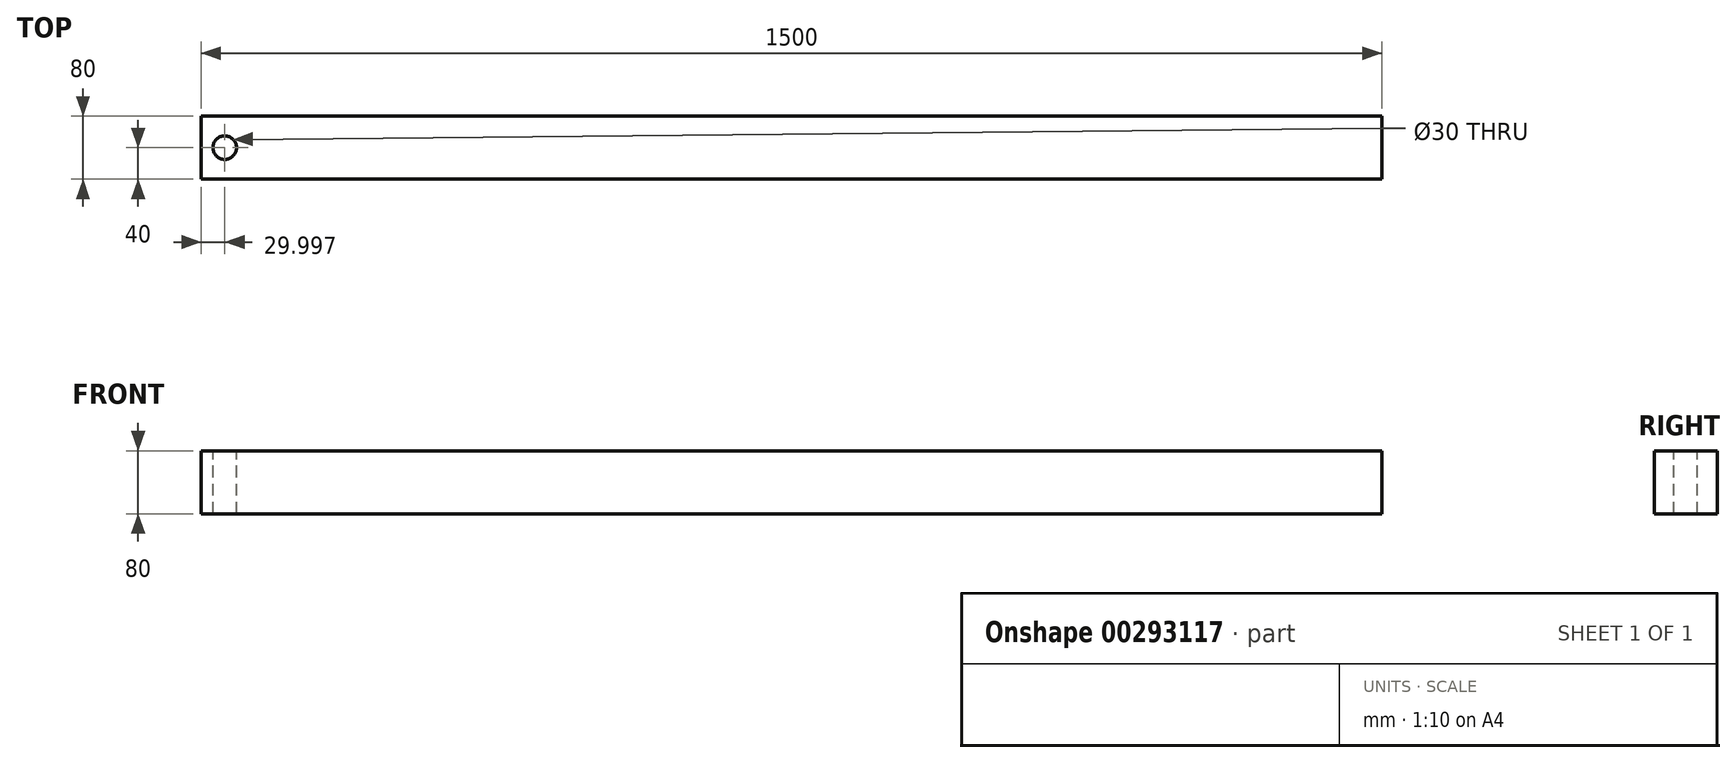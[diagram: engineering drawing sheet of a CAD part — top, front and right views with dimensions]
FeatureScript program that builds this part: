
annotation { "Feature Type Name" : "Feature", "Feature Type Description" : "" }
export const myFeature = defineFeature(function(context is Context, id is Id, definition is map)
    precondition{}
    {
        {
            var Q0;
            Q0=qCreatedBy(makeId("Top.planeOp"),FACE);
            var sketch = newSketch(context, id + "F0", { "sketchPlane" : qUnion([Q0])});
            skLineSegment(sketch, "E0.bottom", {"start": v(752.79, -40) * mm, "end": v(-747.21, -40) * mm});
            skLineSegment(sketch, "E0.top", {"start": v(752.79, 40) * mm, "end": v(-747.21, 40) * mm});
            skLineSegment(sketch, "E0.left", {"start": v(752.79, -40) * mm, "end": v(752.79, 40) * mm});
            skLineSegment(sketch, "E0.right", {"start": v(-747.21, -40) * mm, "end": v(-747.21, 40) * mm});
            skPoint(sketch, "E0.middle", {"position": v(2.79, 0) * mm});
            skSolve(sketch);
        }
        {
            var Q0;
            Q0=makeQuery(id+"F0.imprint","IMPRINT",FACE,{"disambiguationData":[TD([[makeQuery(id+"F0.imprint","IMPRINT",EDGE,{"derivedFrom":sQuery(id+"F0.wireOp",EDGE,"E0.bottom")}),-1.0]])]});
            extrude(context, id + "F1", {"entities" : qUnion([Q0]), "depth" : 80 * mm});
        }
        {
            var Q0;
            Q0=makeQuery(id+"F1.opExtrude","CAP_FACE",FACE,{"disambiguationData":[OSD([sQuery(id+"F0.wireOp",EDGE,"E0.bottom"),sQuery(id+"F0.wireOp",EDGE,"E0.top"),sQuery(id+"F0.wireOp",EDGE,"E0.left"),sQuery(id+"F0.wireOp",EDGE,"E0.right")])],"isStart":false});
            var sketch = newSketch(context, id + "F2", { "sketchPlane" : qUnion([Q0])});
            skPoint(sketch, "E1", {"position": v(-717.21, 0) * mm});
            skPoint(sketch, "E1.positionSnap0", {"position": v(-747.21, 0) * mm});
            skCircle(sketch, "E2", {"center": v(-717.21, 0) * mm, "radius": 15 * mm});
            skSolve(sketch);
        }
        {
            var Q0;
            Q0=makeQuery(id+"F2.imprint","IMPRINT",FACE,{"disambiguationData":[TD([[makeQuery(id+"F2.imprint","IMPRINT",EDGE,{"derivedFrom":sQuery(id+"F2.wireOp",EDGE,"E2")}),1.0]])]});
            extrude(context, id + "F3", {"entities" : qUnion([Q0]), "operationType" : NewBodyOperationType.REMOVE, "endBound" : BoundingType.THROUGH_ALL, "oppositeDirection" : true, "depth" : 25 * mm});
        }
    });
